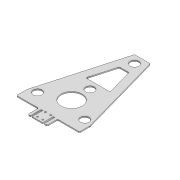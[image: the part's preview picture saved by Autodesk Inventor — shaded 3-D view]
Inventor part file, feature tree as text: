
AUTODESK INVENTOR PART (.ipt)
format: ipt  version: 2022 (Build 260153000, 153)  size: 294,912 bytes
history: native  units: mm
features: extrude x4, sketch x4, projected_geometry x3, fillet x1
ambient origin geometry x8: Origin, YZ Plane, XZ Plane, XY Plane, X Axis, Y Axis, Z Axis, Center Point
bodies: Solid1 (feature_tree)
feature tree (12):
  extrude  "Extrusion1"  Depth=20.0mm
  fillet  "Fillet1"  Radius=120.0mm
  sketch  "Sketch6"  dims[d3=60.0mm d4=20.0mm]
  sketch  "Sketch7"  dims[d6=200.0mm d7=45.0mm]
  extrude  "Extrusion3"  Depth=20.0mm
  extrude  "Extrusion4"  Depth=200.0mm
  extrude  "Extrusion5"  Depth=5.0mm
  sketch  "Sketch1"  dims[d0=20.0mm d1=20.0mm d2=120.0mm]
  projected_geometry  "Projected Loop4"
  projected_geometry  "Projected Loop5"
  sketch  "Sketch8"  dims[d8=45.0mm d9=16.5mm d10=16.5mm d11=16.5mm d12=16.5mm d13=15.0mm d14=15.0mm d15=25.0mm d16=25.0mm d17=15.0mm d18=100.0mm d23=3.0mm d24=3.0mm d25=3.0mm d26=3.0mm d27=5.0mm d28=5.0mm d29=5.0mm d30=5.0mm d31=0.0mm d32=0.0mm d33=5.0mm d34=5.0mm d35=2.0mm d36=0.0mm d37=2.0mm d38=3.1mm d39=3.1mm d40=5.0mm d41=5.0mm d56=15.0mm d57=15.0mm d58=20.0mm d59=15.0mm d64=40.0mm d66=35.0mm d67=16.2mm d68=16.2mm d69=16.2mm d70=16.2mm d71=3.0mm d72=3.0mm d73=3.0mm d74=3.0mm d75=5.0mm d76=0.0mm d77=30.0mm d78=0.0mm d79=0.1mm d80=0.1mm d81=0.1mm d82=0.1mm d83=30.0mm d84=0.0mm]
  projected_geometry  "Projected Loop6"
